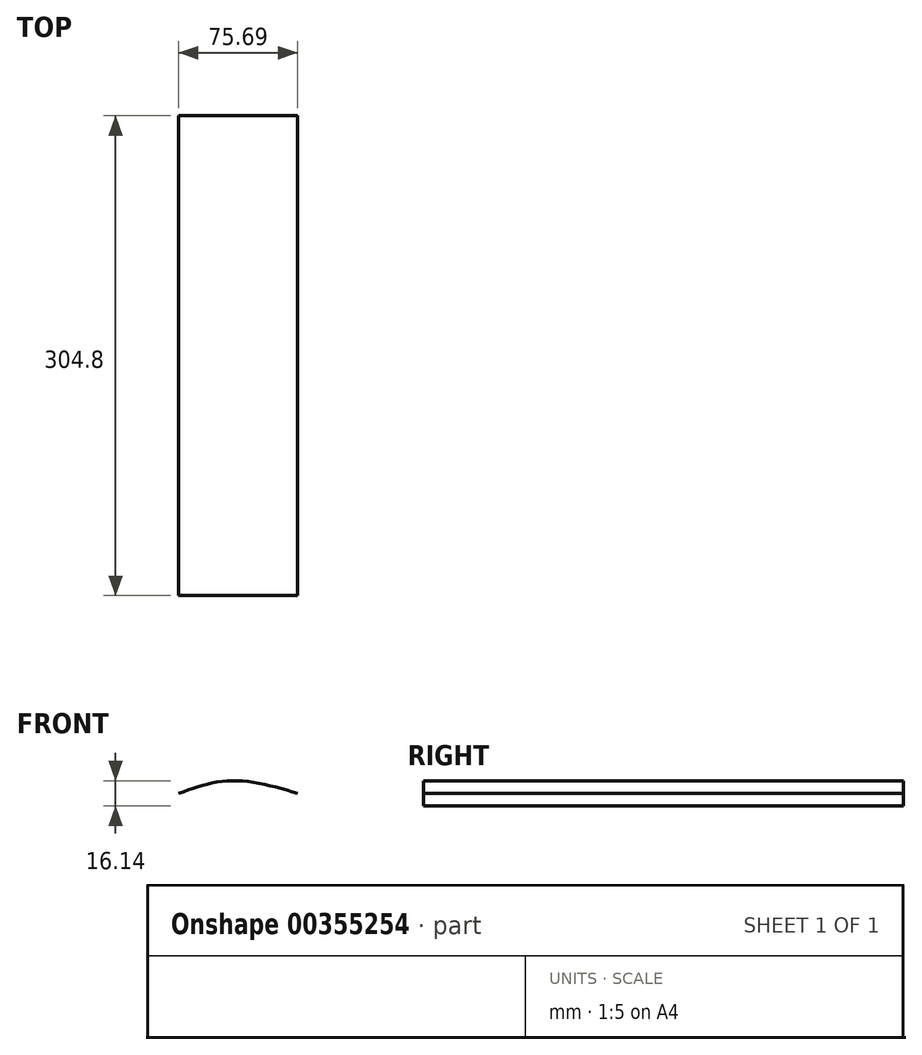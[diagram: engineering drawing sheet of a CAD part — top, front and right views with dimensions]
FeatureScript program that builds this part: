
annotation { "Feature Type Name" : "Feature", "Feature Type Description" : "" }
export const myFeature = defineFeature(function(context is Context, id is Id, definition is map)
    precondition{}
    {
        {
            var Q0;
            Q0=qCreatedBy(makeId("Front.planeOp"),FACE);
            var sketch = newSketch(context, id + "F0", { "sketchPlane" : qUnion([Q0])});
            skFitSpline(sketch, "E0", {"points": [v(0, 0) * mm, v(33.81, 8.06) * mm, v(75.69, 0) * mm], "startDerivative": vector(69.27, 24.66) * mm, "endDerivative": vector(81.89, -23.83) * mm});
            skFitSpline(sketch, "E1.MirrorCS", {"points": [v(0, 0) * mm, v(33.81, -8.06) * mm, v(75.69, 0) * mm], "startDerivative": vector(69.27, -24.66) * mm, "endDerivative": vector(81.89, 23.83) * mm});
            skSolve(sketch);
        }
        {
            var Q0;
            Q0 = qSketchRegion(id + "F0", true);
            extrude(context, id + "F1", {"entities" : qUnion([Q0]), "depth" : 304.8 * mm});
        }
    });
